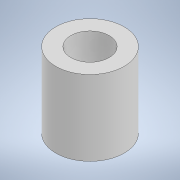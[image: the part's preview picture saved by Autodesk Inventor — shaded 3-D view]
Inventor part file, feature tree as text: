
AUTODESK INVENTOR PART (.ipt)
format: ipt  version: 2022.3 (Build 263350000, 350)  size: 98,304 bytes
history: native  units: mm
features: extrude x1, sketch x1
ambient origin geometry x8: Origin, YZ Plane, XZ Plane, XY Plane, X Axis, Y Axis, Z Axis, Center Point
bodies: Solid1 (feature_tree)
feature tree (2):
  extrude  "Extrusion1"  Depth=10.0mm
  sketch  "Sketch1"  dims[d0=5.1mm d1=2.0mm d2=10.0mm d3=0.0mm]
